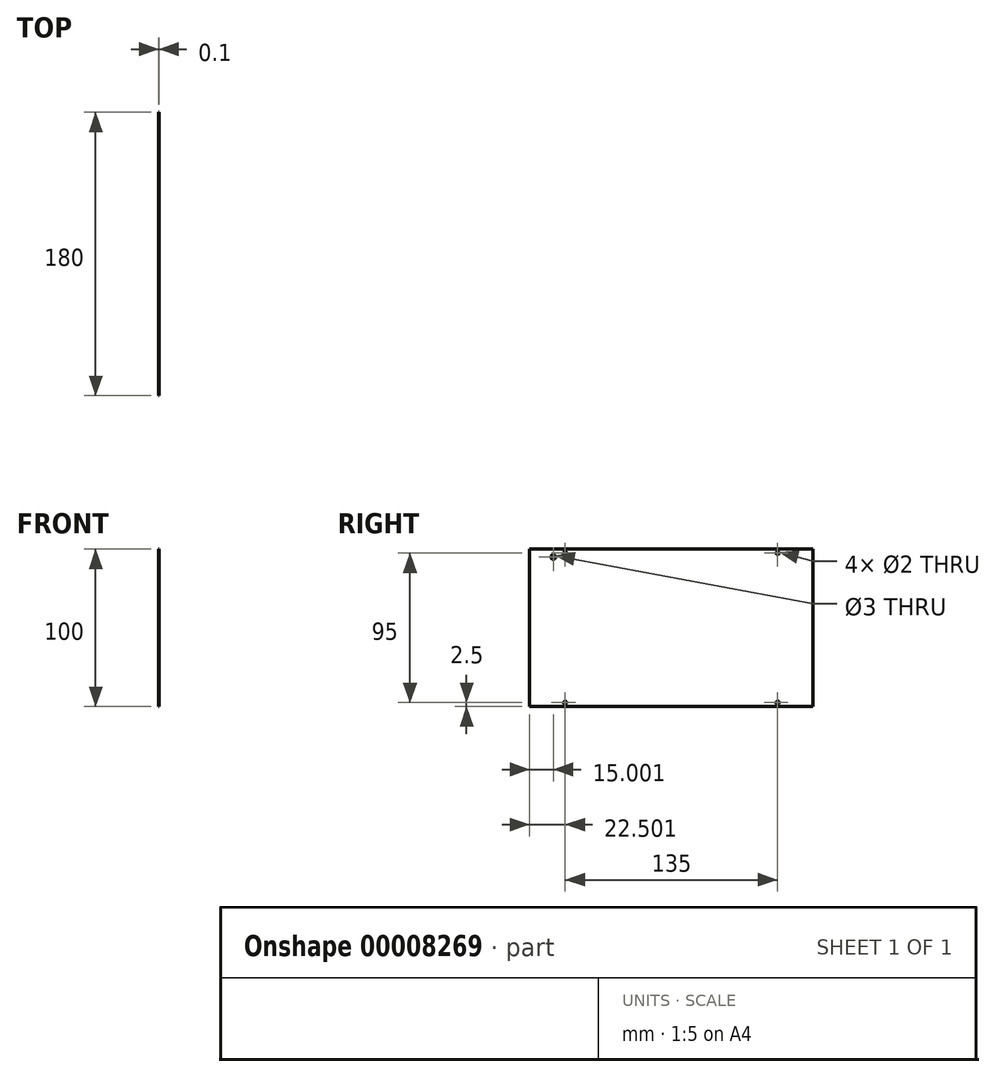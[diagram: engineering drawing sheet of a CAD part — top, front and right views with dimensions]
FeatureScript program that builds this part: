
annotation { "Feature Type Name" : "Feature", "Feature Type Description" : "" }
export const myFeature = defineFeature(function(context is Context, id is Id, definition is map)
    precondition{}
    {
        {
            var Q0;
            Q0=qCreatedBy(makeId("Right.planeOp"),FACE);
            var sketch = newSketch(context, id + "F0", { "sketchPlane" : qUnion([Q0])});
            skLineSegment(sketch, "E0.bottom", {"start": v(-71.1, 34.4) * mm, "end": v(108.9, 34.4) * mm});
            skLineSegment(sketch, "E0.top", {"start": v(-71.1, -65.6) * mm, "end": v(108.9, -65.6) * mm});
            skLineSegment(sketch, "E0.left", {"start": v(-71.1, 34.4) * mm, "end": v(-71.1, -65.6) * mm});
            skLineSegment(sketch, "E0.right", {"start": v(108.9, 34.4) * mm, "end": v(108.9, -65.6) * mm});
            skCircle(sketch, "E1", {"center": v(-48.6, 31.9) * mm, "radius": 1 * mm});
            skPoint(sketch, "E2", {"position": v(18.9, 34.4) * mm});
            skLineSegment(sketch, "E3", {"start": v(18.9, 34.4) * mm, "end": v(18.9, -65.6) * mm, "construction": true});
            skLineSegment(sketch, "E4", {"start": v(18.9, -65.6) * mm, "end": v(18.9, -15.6) * mm, "construction": true});
            skLineSegment(sketch, "E5", {"start": v(108.9, -15.6) * mm, "end": v(-71.1, -15.6) * mm, "construction": true});
            skCircle(sketch, "E6.0.MirrorC", {"center": v(86.4, 31.9) * mm, "radius": 1 * mm});
            skCircle(sketch, "E7.0.MirrorC", {"center": v(86.4, -63.1) * mm, "radius": 1 * mm});
            skCircle(sketch, "E8.0.MirrorC", {"center": v(-48.6, -63.1) * mm, "radius": 1 * mm});
            skCircle(sketch, "E9", {"center": v(-56.1, 29.4) * mm, "radius": 1.5 * mm});
            skSolve(sketch);
        }
        {
            var Q0;
            Q0 = qSketchRegion(id + "F0", true);
            extrude(context, id + "F1", {"entities" : qUnion([Q0]), "depth" : 0.1 * mm});
        }
    });
